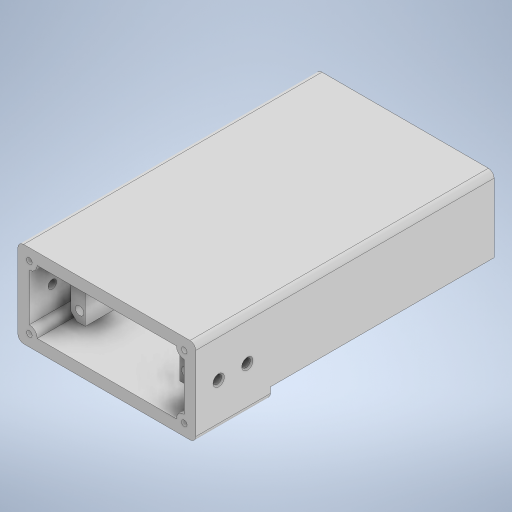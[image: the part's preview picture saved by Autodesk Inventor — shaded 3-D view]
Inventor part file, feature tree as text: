
AUTODESK INVENTOR PART (.ipt)
format: ipt  version: 2023.1 (Build 271208000, 208)  size: 493,568 bytes
history: native  units: mm
features: extrude x15, sketch x11, fillet x3, chamfer x3, projected_geometry x2, other x1, mirror x1
ambient origin geometry x8: Origin, YZ Plane, XZ Plane, XY Plane, X Axis, Y Axis, Z Axis, Center Point
bodies: Body1 (feature_tree)
feature tree (36):
  other  "솔리드1"
  sketch  "스케치1"
  extrude  "돌출1"  Depth=54.0mm
  extrude  "돌출2"  Depth=22.0mm
  sketch  "스케치2"
  extrude  "돌출3"  Depth=20.0mm
  fillet  "모깎기1"  Radius=10.0mm
  extrude  "돌출4"  Depth=30.0mm
  sketch  "스케치3"
  extrude  "돌출5"  Depth=11.0mm
  extrude  "돌출6"  Depth=1.0mm
  chamfer  "모따기1"  Distance=4.0mm
  extrude  "돌출7"  Depth=3.0mm TaperAngle=0.0deg
  extrude  "돌출8"  Depth=75.0mm TaperAngle=0.0deg
  sketch  "스케치6"
  extrude  "돌출9"  Depth=1.0mm
  extrude  "돌출10"  Depth=8.726646mm
  extrude  "돌출11"  Depth=74.0mm TaperAngle=0.0deg
  chamfer  "모따기2"  Distance=0.5mm
  fillet  "모깎기2"  Radius=3.0mm
  extrude  "돌출12"  Depth=25.1mm
  extrude  "돌출13"  Depth=52.1mm
  extrude  "돌출14"  Depth=31.2mm
  fillet  "모깎기4"  Radius=57.6mm
  extrude  "돌출15"  Depth=3.0mm
  mirror  "미러1"
  chamfer  "모따기4"  Distance=5.0mm
  sketch  "스케치4"
  sketch  "스케치5"
  projected_geometry  "투영된 루프1"
  sketch  "스케치7"
  sketch  "스케치8"
  projected_geometry  "투영된 루프2"
  sketch  "스케치9"
  sketch  "스케치10"
  sketch  "스케치14"
